# Revit family: FP-Revit19-en-CIT122DX1-CIT152DX1-TeppanyakiCooktop-0-90003221A-US-CA
name_source: partatom
category: Specialty Equipment
units: mm (PartAtom-declared; Revit-internal decimal feet)

## family parameters
Always vertical = Yes
Cut with Voids When Loaded = Yes
Part Type = Normal
Room Calculation Point = No
Round Connector Dimension = Use Diameter
Shared = No
Work Plane-Based = No

## types (2) — shared parameters
Cavity - Depth (Flush Mount) = 509 mm  [stored 1.66995 ft]
Cavity - Depth (Proud Mount) = 507 mm
Cavity - Height = 87 mm  [stored 0.285433 ft]
Chassis - Depth = 504 mm  [stored 1.65354 ft]
Chassis - Height = 69 mm
Clearance - Overhead Non-Combustible = 450 mm  [stored 1.47638 ft]
Clearance - Overhead Rangehood = 650 mm
Clearance - Rear Combustible = 20 mm
Clearance - Side Combustible = 27 mm  [stored 0.0885827 ft]
Connector Description - Electrical = 120V, 60Hz, 20A
Manufacturer = Fisher & Paykel Appliances Ltd
Material - Body = Fisher & Paykel - Stainless Steel
Material - Teppanyaki = Fisher & Paykel - Stainless Steel
Product - Depth = 530 mm  [stored 1.73885 ft]
Product - Height = 74 mm
Visibility - Clearance Required = Yes

## per-type parameters (varying)
| type | Cavity - Width | Chassis - Width | Description | Product - Width |
| CIT122DX1 | 260 mm | 251 mm  [stored 0.823491 ft] | Auxiliary Modular Teppanyaki Cooktop, 12" | 300 mm |
| CIT152DX1 | 347 mm | 336 mm  [stored 1.10236 ft] | Auxiliary Modular Teppanyaki Cooktop, 15" | 385 mm |

note: column(s) folded — value = type name in every type: Model

note: [stored X ft] marks values corroborated as IEEE doubles in the binary element streams (Revit-internal decimal feet)

## geometry (parser evidence)
native form markers: Sweep x3
no freeform markers — native parametric forms only
